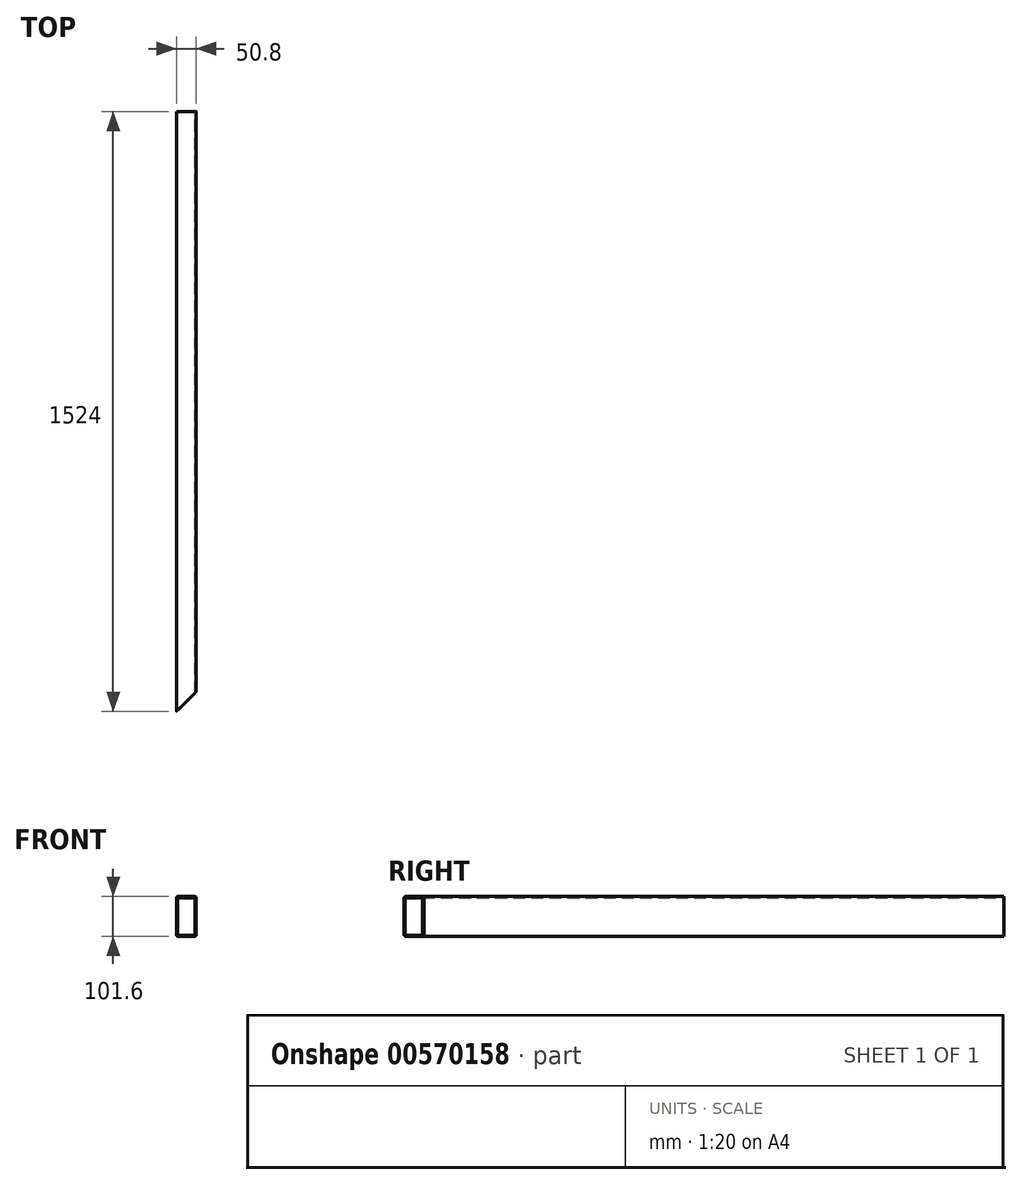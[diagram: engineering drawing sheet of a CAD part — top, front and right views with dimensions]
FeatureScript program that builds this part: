
annotation { "Feature Type Name" : "Feature", "Feature Type Description" : "" }
export const myFeature = defineFeature(function(context is Context, id is Id, definition is map)
    precondition{}
    {
        {
            var Q0;
            Q0=qCreatedBy(makeId("Front.planeOp"),FACE);
            var sketch = newSketch(context, id + "F0", { "sketchPlane" : qUnion([Q0])});
            skLineSegment(sketch, "E0.bottom", {"start": v(0, 0) * mm, "end": v(50.8, 0) * mm});
            skLineSegment(sketch, "E0.top", {"start": v(0, 101.6) * mm, "end": v(50.8, 101.6) * mm});
            skLineSegment(sketch, "E0.left", {"start": v(0, 0) * mm, "end": v(0, 101.6) * mm});
            skLineSegment(sketch, "E0.right", {"start": v(50.8, 0) * mm, "end": v(50.8, 101.6) * mm});
            skLineSegment(sketch, "E1.bottom", {"start": v(3.17, 98.42) * mm, "end": v(47.62, 98.42) * mm});
            skLineSegment(sketch, "E1.top", {"start": v(3.17, 3.18) * mm, "end": v(47.63, 3.18) * mm});
            skLineSegment(sketch, "E1.left", {"start": v(3.17, 98.42) * mm, "end": v(3.18, 3.17) * mm});
            skLineSegment(sketch, "E1.right", {"start": v(47.62, 98.42) * mm, "end": v(47.63, 3.17) * mm});
            skSolve(sketch);
        }
        {
            var Q0;
            Q0=makeQuery(id+"F0.imprint","IMPRINT",FACE,{"disambiguationData":[TD([[makeQuery(id+"F0.imprint","IMPRINT",EDGE,{"derivedFrom":sQuery(id+"F0.wireOp",EDGE,"E0.bottom")}),1.0]])]});
            extrude(context, id + "F1", {"entities" : qUnion([Q0]), "depth" : 1524 * mm, "offsetDistance" : 25.4 * mm});
        }
        {
            var Q0;
            Q0=makeQuery(id+"F1.opExtrude","SWEPT_FACE",FACE,{"disambiguationData":[OSD([sQuery(id+"F0.wireOp",EDGE,"E0.top")])]});
            var sketch = newSketch(context, id + "F2", { "sketchPlane" : qUnion([Q0])});
            skLineSegment(sketch, "E2", {"start": v(0, -1524) * mm, "end": v(50.8, -1473.2) * mm});
            skLineSegment(sketch, "E3", {"start": v(0, -1524) * mm, "end": v(50.8, -1524) * mm});
            skLineSegment(sketch, "E4", {"start": v(50.8, -1524) * mm, "end": v(50.8, -1473.2) * mm});
            skSolve(sketch);
        }
        {
            var Q0;
            Q0=makeQuery(id+"F2.imprint","IMPRINT",FACE,{"disambiguationData":[TD([[makeQuery(id+"F2.imprint","IMPRINT",EDGE,{"derivedFrom":sQuery(id+"F2.wireOp",EDGE,"oG9oAAjW-ZJQ0-wkjL-ms8t-89WF7IWCZLWI")}),1.0]])]});
            var Q1;
            Q1=makeQuery(id+"F2.imprint","IMPRINT",FACE,{"disambiguationData":[TD([[makeQuery(id+"F2.imprint","IMPRINT",EDGE,{"derivedFrom":sQuery(id+"F2.wireOp",EDGE,"E2")}),-1.0]])]});
            extrude(context, id + "F3", {"entities" : qUnion([Q0, Q1]), "operationType" : NewBodyOperationType.REMOVE, "oppositeDirection" : true, "depth" : 173.23 * mm, "offsetDistance" : 25.4 * mm});
        }
        {
            var Q0;
            Q0=makeQuery(id+"F1.opExtrude","SWEPT_EDGE",EDGE,{"disambiguationData":[OSD([sQuery(id+"F0.wireOp",EDGE,"E0.bottom"),sQuery(id+"F0.wireOp",EDGE,"E0.left")])]});
            var Q1;
            Q1=makeQuery(id+"F1.opExtrude","SWEPT_EDGE",EDGE,{"disambiguationData":[OSD([sQuery(id+"F0.wireOp",EDGE,"E0.bottom"),sQuery(id+"F0.wireOp",EDGE,"E0.right")])]});
            var Q2;
            Q2=makeQuery(id+"F1.opExtrude","SWEPT_EDGE",EDGE,{"disambiguationData":[OSD([sQuery(id+"F0.wireOp",EDGE,"E0.top"),sQuery(id+"F0.wireOp",EDGE,"E0.right")])]});
            var Q3;
            Q3=makeQuery(id+"F1.opExtrude","SWEPT_EDGE",EDGE,{"disambiguationData":[OSD([sQuery(id+"F0.wireOp",EDGE,"E0.top"),sQuery(id+"F0.wireOp",EDGE,"E0.left")])]});
            fillet(context, id + "F4", {"entities" : qUnion([Q0, Q1, Q2, Q3]), "radius" : 5.08 * mm, "tangentPropagation" : true, "allowEdgeOverflow" : false});
        }
    });
